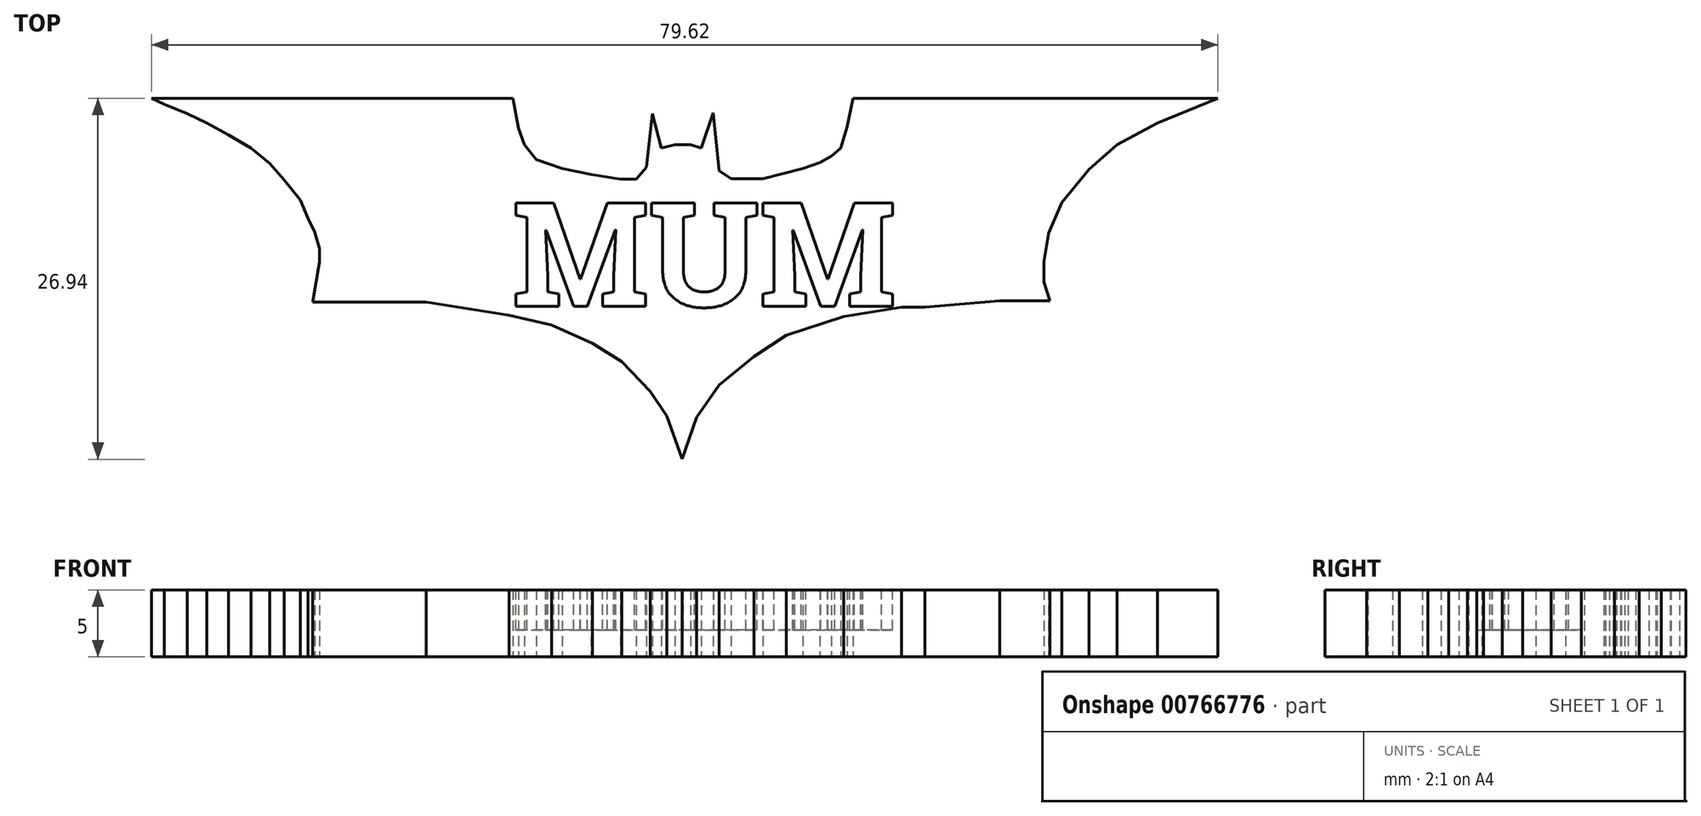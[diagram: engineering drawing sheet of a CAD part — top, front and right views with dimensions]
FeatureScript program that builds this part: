
annotation { "Feature Type Name" : "Feature", "Feature Type Description" : "" }
export const myFeature = defineFeature(function(context is Context, id is Id, definition is map)
    precondition{}
    {
        {
            var Q0;
            Q0=qCreatedBy(makeId("Top.planeOp"),FACE);
            var sketch = newSketch(context, id + "F0", { "sketchPlane" : qUnion([Q0])});
            skLineSegment(sketch, "E0", {"start": v(-18, -9.17) * mm, "end": v(-44.99, -9.17) * mm});
            skLineSegment(sketch, "E1", {"start": v(-44.99, -9.17) * mm, "end": v(-44.05, -9.62) * mm});
            skLineSegment(sketch, "E2", {"start": v(-44.05, -9.62) * mm, "end": v(-42.31, -10.31) * mm});
            skLineSegment(sketch, "E3", {"start": v(-42.31, -10.31) * mm, "end": v(-40.88, -11) * mm});
            skLineSegment(sketch, "E4", {"start": v(-40.88, -11) * mm, "end": v(-39.24, -11.9) * mm});
            skLineSegment(sketch, "E5", {"start": v(-39.24, -11.9) * mm, "end": v(-37.56, -12.89) * mm});
            skLineSegment(sketch, "E6", {"start": v(-37.56, -12.89) * mm, "end": v(-36.17, -14.03) * mm});
            skLineSegment(sketch, "E7", {"start": v(-36.17, -14.03) * mm, "end": v(-35.08, -15.26) * mm});
            skLineSegment(sketch, "E8", {"start": v(-35.08, -15.26) * mm, "end": v(-33.9, -16.75) * mm});
            skLineSegment(sketch, "E9", {"start": v(-33.9, -16.75) * mm, "end": v(-33.3, -18.14) * mm});
            skLineSegment(sketch, "E10", {"start": v(-33.3, -18.14) * mm, "end": v(-32.8, -19.18) * mm});
            skLineSegment(sketch, "E11", {"start": v(-32.8, -19.18) * mm, "end": v(-32.46, -20.36) * mm});
            skLineSegment(sketch, "E12", {"start": v(-32.46, -20.36) * mm, "end": v(-32.46, -21.4) * mm});
            skLineSegment(sketch, "E13", {"start": v(-32.46, -21.4) * mm, "end": v(-32.96, -24.37) * mm});
            skLineSegment(sketch, "E14", {"start": v(-32.96, -24.37) * mm, "end": v(-30.68, -24.37) * mm});
            skLineSegment(sketch, "E15", {"start": v(-30.68, -24.37) * mm, "end": v(-28.4, -24.37) * mm});
            skLineSegment(sketch, "E16", {"start": v(-28.4, -24.37) * mm, "end": v(-24.49, -24.37) * mm});
            skLineSegment(sketch, "E17", {"start": v(-24.49, -24.37) * mm, "end": v(-22.01, -24.77) * mm});
            skLineSegment(sketch, "E18", {"start": v(-22.01, -24.77) * mm, "end": v(-18.3, -25.37) * mm});
            skLineSegment(sketch, "E19", {"start": v(-18.3, -25.37) * mm, "end": v(-15.13, -26.1) * mm});
            skLineSegment(sketch, "E20", {"start": v(-15.13, -26.1) * mm, "end": v(-12.06, -27.44) * mm});
            skLineSegment(sketch, "E21", {"start": v(-12.06, -27.44) * mm, "end": v(-9.88, -28.83) * mm});
            skLineSegment(sketch, "E22", {"start": v(-9.88, -28.83) * mm, "end": v(-7.75, -31.06) * mm});
            skLineSegment(sketch, "E23", {"start": v(-7.75, -31.06) * mm, "end": v(-6.51, -32.9) * mm});
            skLineSegment(sketch, "E24", {"start": v(-6.51, -32.9) * mm, "end": v(-5.37, -36.1) * mm});
            skLineSegment(sketch, "E25", {"start": v(-5.37, -36.1) * mm, "end": v(-4.29, -33) * mm});
            skLineSegment(sketch, "E26", {"start": v(-4.29, -33) * mm, "end": v(-2.6, -30.56) * mm});
            skLineSegment(sketch, "E27", {"start": v(-2.6, -30.56) * mm, "end": v(0, -28.44) * mm});
            skLineSegment(sketch, "E28", {"start": v(0, -28.44) * mm, "end": v(2.4, -26.85) * mm});
            skLineSegment(sketch, "E29", {"start": v(2.4, -26.85) * mm, "end": v(6.7, -25.46) * mm});
            skLineSegment(sketch, "E30", {"start": v(6.7, -25.46) * mm, "end": v(11.01, -24.77) * mm});
            skLineSegment(sketch, "E31", {"start": v(11.01, -24.77) * mm, "end": v(12.75, -24.77) * mm});
            skLineSegment(sketch, "E32", {"start": v(12.75, -24.77) * mm, "end": v(18.34, -24.28) * mm});
            skLineSegment(sketch, "E33", {"start": v(18.34, -24.28) * mm, "end": v(22.1, -24.28) * mm});
            skLineSegment(sketch, "E34", {"start": v(22.1, -24.28) * mm, "end": v(21.65, -22.88) * mm});
            skLineSegment(sketch, "E35", {"start": v(21.65, -22.88) * mm, "end": v(21.65, -21.35) * mm});
            skLineSegment(sketch, "E36", {"start": v(21.65, -21.35) * mm, "end": v(22, -19.23) * mm});
            skLineSegment(sketch, "E37", {"start": v(22, -19.23) * mm, "end": v(23, -16.95) * mm});
            skLineSegment(sketch, "E38", {"start": v(23, -16.95) * mm, "end": v(25.03, -14.47) * mm});
            skLineSegment(sketch, "E39", {"start": v(25.03, -14.47) * mm, "end": v(27.1, -12.64) * mm});
            skLineSegment(sketch, "E40", {"start": v(27.1, -12.64) * mm, "end": v(30.13, -11) * mm});
            skLineSegment(sketch, "E41", {"start": v(30.13, -11) * mm, "end": v(34.63, -9.17) * mm});
            skLineSegment(sketch, "E42", {"start": v(-18, -9.17) * mm, "end": v(-17.6, -11.4) * mm});
            skLineSegment(sketch, "E43", {"start": v(-17.6, -11.4) * mm, "end": v(-17.16, -12.64) * mm});
            skLineSegment(sketch, "E44", {"start": v(-17.16, -12.64) * mm, "end": v(-16.27, -13.73) * mm});
            skLineSegment(sketch, "E45", {"start": v(-16.27, -13.73) * mm, "end": v(-14.34, -14.42) * mm});
            skLineSegment(sketch, "E46", {"start": v(-14.34, -14.42) * mm, "end": v(-12.16, -14.87) * mm});
            skLineSegment(sketch, "E47", {"start": v(-12.16, -14.87) * mm, "end": v(-9.98, -15.21) * mm});
            skLineSegment(sketch, "E48", {"start": v(-9.98, -15.21) * mm, "end": v(-8.8, -15.21) * mm});
            skLineSegment(sketch, "E49", {"start": v(-8.8, -15.21) * mm, "end": v(-8.05, -14.32) * mm});
            skLineSegment(sketch, "E50", {"start": v(-8.05, -14.32) * mm, "end": v(-7.6, -10.31) * mm});
            skLineSegment(sketch, "E51", {"start": v(-7.6, -10.31) * mm, "end": v(-6.91, -12.89) * mm});
            skLineSegment(sketch, "E52", {"start": v(-6.91, -12.89) * mm, "end": v(-5.93, -12.62) * mm});
            skLineSegment(sketch, "E53", {"start": v(-5.93, -12.62) * mm, "end": v(-4.73, -12.62) * mm});
            skLineSegment(sketch, "E54", {"start": v(-4.73, -12.62) * mm, "end": v(-3.94, -12.89) * mm});
            skLineSegment(sketch, "E55", {"start": v(-3.94, -12.89) * mm, "end": v(-3.06, -10.26) * mm});
            skLineSegment(sketch, "E56", {"start": v(-3.06, -10.26) * mm, "end": v(-2.6, -14.57) * mm});
            skLineSegment(sketch, "E57", {"start": v(-2.6, -14.57) * mm, "end": v(-1.71, -15.17) * mm});
            skLineSegment(sketch, "E58", {"start": v(-1.71, -15.17) * mm, "end": v(0.66, -15.17) * mm});
            skLineSegment(sketch, "E59", {"start": v(0.66, -15.17) * mm, "end": v(3.64, -14.42) * mm});
            skLineSegment(sketch, "E60", {"start": v(3.64, -14.42) * mm, "end": v(4.92, -13.98) * mm});
            skLineSegment(sketch, "E61", {"start": v(4.92, -13.98) * mm, "end": v(5.76, -13.48) * mm});
            skLineSegment(sketch, "E62", {"start": v(5.76, -13.48) * mm, "end": v(6.46, -12.89) * mm});
            skLineSegment(sketch, "E63", {"start": v(6.46, -12.89) * mm, "end": v(6.95, -11.3) * mm});
            skLineSegment(sketch, "E64", {"start": v(6.95, -11.3) * mm, "end": v(7.4, -9.17) * mm});
            skLineSegment(sketch, "E65", {"start": v(7.4, -9.17) * mm, "end": v(34.63, -9.17) * mm});
            skSolve(sketch);
        }
        {
            var Q0;
            Q0=makeQuery(id+"F0.imprint","IMPRINT",FACE,{"disambiguationData":[TD([[makeQuery(id+"F0.imprint","IMPRINT",EDGE,{"derivedFrom":sQuery(id+"F0.wireOp",EDGE,"E0")}),1.0]])]});
            extrude(context, id + "F1", {"entities" : qUnion([Q0]), "depth" : 5 * mm, "offsetDistance" : 25 * mm});
        }
        {
            var Q0;
            Q0=makeQuery(id+"F1.opExtrude","CAP_FACE",FACE,{"disambiguationData":[OSD([sQuery(id+"F0.wireOp",EDGE,"E0"),sQuery(id+"F0.wireOp",EDGE,"E1"),sQuery(id+"F0.wireOp",EDGE,"E2"),sQuery(id+"F0.wireOp",EDGE,"E3"),sQuery(id+"F0.wireOp",EDGE,"E4"),sQuery(id+"F0.wireOp",EDGE,"E5"),sQuery(id+"F0.wireOp",EDGE,"E6"),sQuery(id+"F0.wireOp",EDGE,"E7"),sQuery(id+"F0.wireOp",EDGE,"E8"),sQuery(id+"F0.wireOp",EDGE,"E9"),sQuery(id+"F0.wireOp",EDGE,"E10"),sQuery(id+"F0.wireOp",EDGE,"E11"),sQuery(id+"F0.wireOp",EDGE,"E12"),sQuery(id+"F0.wireOp",EDGE,"E13"),sQuery(id+"F0.wireOp",EDGE,"E14"),sQuery(id+"F0.wireOp",EDGE,"E15"),sQuery(id+"F0.wireOp",EDGE,"E16"),sQuery(id+"F0.wireOp",EDGE,"E17"),sQuery(id+"F0.wireOp",EDGE,"E18"),sQuery(id+"F0.wireOp",EDGE,"E19"),sQuery(id+"F0.wireOp",EDGE,"E20"),sQuery(id+"F0.wireOp",EDGE,"E21"),sQuery(id+"F0.wireOp",EDGE,"E22"),sQuery(id+"F0.wireOp",EDGE,"E23"),sQuery(id+"F0.wireOp",EDGE,"E24"),sQuery(id+"F0.wireOp",EDGE,"E25"),sQuery(id+"F0.wireOp",EDGE,"E26"),sQuery(id+"F0.wireOp",EDGE,"E27"),sQuery(id+"F0.wireOp",EDGE,"E28"),sQuery(id+"F0.wireOp",EDGE,"E29"),sQuery(id+"F0.wireOp",EDGE,"E30"),sQuery(id+"F0.wireOp",EDGE,"E31"),sQuery(id+"F0.wireOp",EDGE,"E32"),sQuery(id+"F0.wireOp",EDGE,"E33"),sQuery(id+"F0.wireOp",EDGE,"E34"),sQuery(id+"F0.wireOp",EDGE,"E35"),sQuery(id+"F0.wireOp",EDGE,"E36"),sQuery(id+"F0.wireOp",EDGE,"E37"),sQuery(id+"F0.wireOp",EDGE,"E38"),sQuery(id+"F0.wireOp",EDGE,"E39"),sQuery(id+"F0.wireOp",EDGE,"E40"),sQuery(id+"F0.wireOp",EDGE,"E41"),sQuery(id+"F0.wireOp",EDGE,"E42"),sQuery(id+"F0.wireOp",EDGE,"E43"),sQuery(id+"F0.wireOp",EDGE,"E44"),sQuery(id+"F0.wireOp",EDGE,"E45"),sQuery(id+"F0.wireOp",EDGE,"E46"),sQuery(id+"F0.wireOp",EDGE,"E47"),sQuery(id+"F0.wireOp",EDGE,"E48"),sQuery(id+"F0.wireOp",EDGE,"E49"),sQuery(id+"F0.wireOp",EDGE,"E50"),sQuery(id+"F0.wireOp",EDGE,"E51"),sQuery(id+"F0.wireOp",EDGE,"E52"),sQuery(id+"F0.wireOp",EDGE,"E53"),sQuery(id+"F0.wireOp",EDGE,"E54"),sQuery(id+"F0.wireOp",EDGE,"E55"),sQuery(id+"F0.wireOp",EDGE,"E56"),sQuery(id+"F0.wireOp",EDGE,"E57"),sQuery(id+"F0.wireOp",EDGE,"E58"),sQuery(id+"F0.wireOp",EDGE,"E59"),sQuery(id+"F0.wireOp",EDGE,"E60"),sQuery(id+"F0.wireOp",EDGE,"E61"),sQuery(id+"F0.wireOp",EDGE,"E62"),sQuery(id+"F0.wireOp",EDGE,"E63"),sQuery(id+"F0.wireOp",EDGE,"E64"),sQuery(id+"F0.wireOp",EDGE,"E65")])],"isStart":false});
            var sketch = newSketch(context, id + "F2", { "sketchPlane" : qUnion([Q0])});
            skText(sketch, "E66", { "text": "MUM", "fontName": "RobotoSlab-Bold.ttf"});
            const initialGuessF2  = {"E66": [-0.01809, -0.0247, 1, 0, 0.00783]};
            skSetInitialGuess(sketch, initialGuessF2);
            skSolve(sketch);
        }
        {
            var Q0;
            Q0 = qSketchRegion(id + "F2", true);
            extrude(context, id + "F3", {"entities" : qUnion([Q0]), "operationType" : NewBodyOperationType.REMOVE, "oppositeDirection" : true, "depth" : 3 * mm, "offsetDistance" : 25 * mm});
        }
    });
